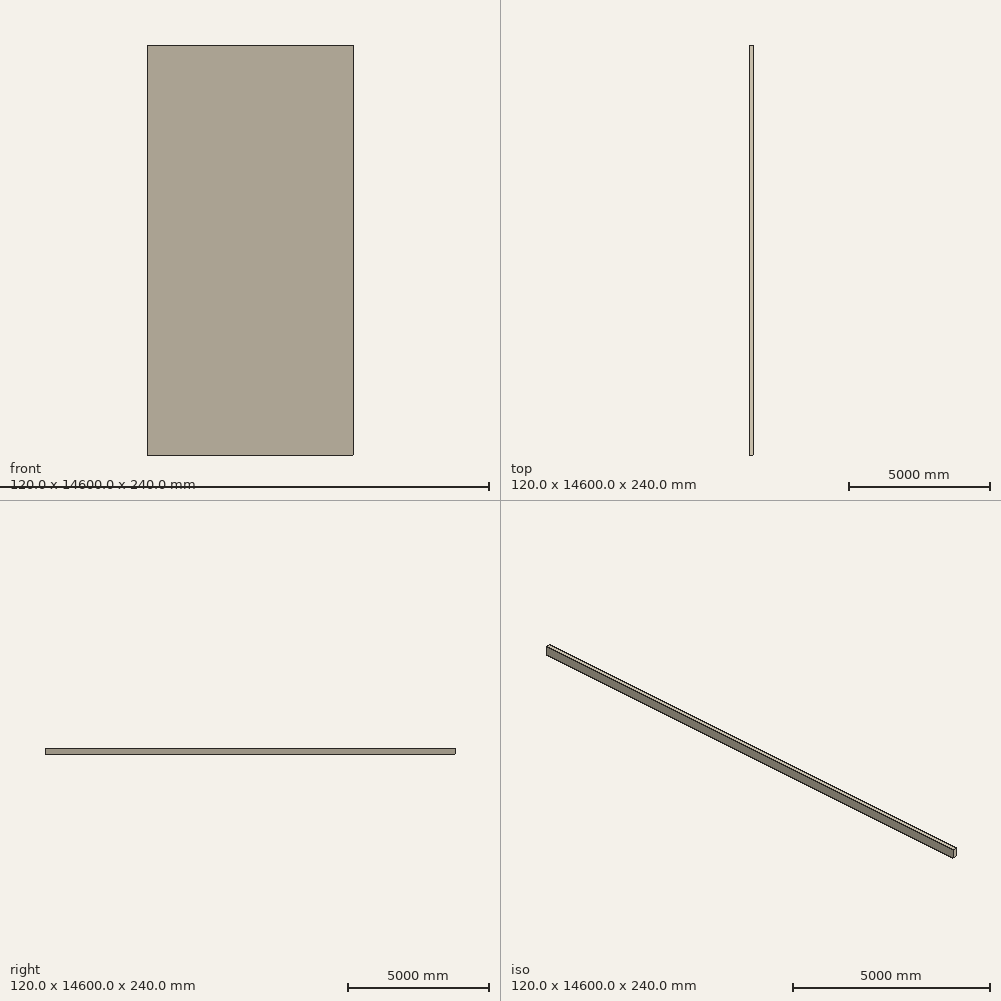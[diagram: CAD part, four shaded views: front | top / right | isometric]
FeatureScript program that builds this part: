
annotation { "Feature Type Name" : "Feature", "Feature Type Description" : "" }
export const myFeature = defineFeature(function(context is Context, id is Id, definition is map)
    precondition{}
    {
        {
            var Q0;
            Q0=qCreatedBy(makeId("Front.planeOp"),FACE);
            var sketch = newSketch(context, id + "F0", { "sketchPlane" : qUnion([Q0])});
            skLineSegment(sketch, "E0.bottom", {"start": v(-18.48, 231.1) * mm, "end": v(101.52, 231.1) * mm});
            skLineSegment(sketch, "E0.top", {"start": v(-18.48, -8.9) * mm, "end": v(101.52, -8.9) * mm});
            skLineSegment(sketch, "E0.left", {"start": v(-18.48, 231.1) * mm, "end": v(-18.48, -8.9) * mm});
            skLineSegment(sketch, "E0.right", {"start": v(101.52, 231.1) * mm, "end": v(101.52, -8.9) * mm});
            skSolve(sketch);
        }
        {
            var Q0;
            Q0=makeQuery(id+"F0.imprint","IMPRINT",FACE,{"disambiguationData":[TD([[makeQuery(id+"F0.imprint","IMPRINT",EDGE,{"derivedFrom":sQuery(id+"F0.wireOp",EDGE,"E0.bottom")}),-1.0]])]});
            var Q1;
            Q1=qSketchRegion(id+"F0",true);
            extrude(context, id + "F1", {"entities" : qUnion([Q0, Q1]), "depth" : 14600 * mm, "offsetDistance" : 25 * mm});
        }
    });
